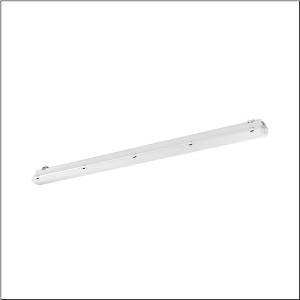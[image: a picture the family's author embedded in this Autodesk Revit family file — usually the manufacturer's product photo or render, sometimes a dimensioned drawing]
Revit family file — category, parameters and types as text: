
# Revit family: monsun_r__11xtreme_mo_51fe10dp440j_05e8
name_source: partatom
category: Lighting Fixtures
units: mm (PartAtom-declared; Revit-internal decimal feet)

## family parameters
Cut with Voids When Loaded = No
Host = Face
Light Source = No
Part Type = Normal
Room Calculation Point = No
Round Connector Dimension = Use Diameter
Shared = No

## types (1)
- --- (1 x LED, 4200 lm, 24.2 W, 4000K)
    Apparent Load = 24 VA
    CIE Flux Codes = 47 77 93 94 100
    Color Rendering = 80
    Color Temperature = 4000K
    Default Elevation = 1800 mm
    Description = Monsun® 11Xtreme MO, damp-proof luminaire, chain hanger, primary optical cover: enclosure, of PMMA, light emission: direct distribution, primary light characteristic: symmetric, installation type: suspended mounting, surface-mounted, horizontal mounting, vertical mounting, LED, rated luminous flux: 4.200lm, luminous efficacy: 174lm/W, light colour: 840, colour temperature: 4000K, control gear: ECG DALI, with terminal, 5-pole, max. 2.5mm², mains connection: 220..240V, AC, 50/60Hz, rated input power: 24W, luminaire housing, of glass-fibre reinforced polyester, uncoated, bright grey, incl. chain hanger, length: 1.590mm, width: 90mm, height: 88mm, clip for enclosure, of stainless steel (V2A), ceiling mounting element, of stainless steel (V2A), chain hanger, of stainless steel (V2A), protection rating (complete): IP66, insulation class (complete): insulation class I (protective earthing), certification: CE, ENEC, VDE, UKCA, protection symbol: D, impact resistance: IK04, permissible operating ambient temperature: -25..+50°C, standard: EN 60598-2-1, EN 50419, corresponds to IFS (International Featured Standards) requirements for safety and quality in the food industry, for indoor or canopied outdoor use, no direct snow, no direct sun, no direct rain, contact your sales advisor before using the luminaires in applications with unclear chemical exposure, large temperature fluctuations or condensation-forming humidity, LABS conformity tested according to VDMA 24364:2018-05, packaging unit: 1 piece
    Height = 88 mm
    Lamp = 1 x LED
    Lamp Light Flux = 4200 lm
    Lamp Power = 24.2 W
    Lamp count = 1
    Length = 1590 mm
    Luminous efficacy = 174 lm/W
    Manufacturer = Siteco
    ModVariant = No
    Model = 51FE10DP440J
    Mounting Place = Ceiling
    Mounting Type = Surface mounted
    Number of Poles = 1
    OnlyDefault = Yes
    Power Factor = 1
    Product Name = Monsun® 11Xtreme MO
    Product group = damp-proof luminaire
    ProductGroupID = 300
    Protection Class = Protection class I
    Protection Degree = IP 66
    RLX_Detail_Level = 1
    RLX_Emergency_Light_Flux = 0 lm
    RLX_Emergency_Type = 0
    RLX_Emergency_Type_DB = No
    RlxData = <blob elided: 87285 chars, md5=9b0b0dc7>
    Socket = socket
    Standby Power = 0 W
    System Light Flux = 4200 lm
    System Power = 24 W
    Type Comments = factory setting: luminous flux: 100 % | dim-lin: 254 | 159 mA
    Type Image = l_1006851.jpg
    URL = http://relux.com
    VarID = @adj_133211
    Voltage = 0 V
    Weight = 0.00 kg
    Width = 90 mm

## geometry (parser evidence)
native form markers: Blend x4, Sweep x12
no freeform markers — native parametric forms only
